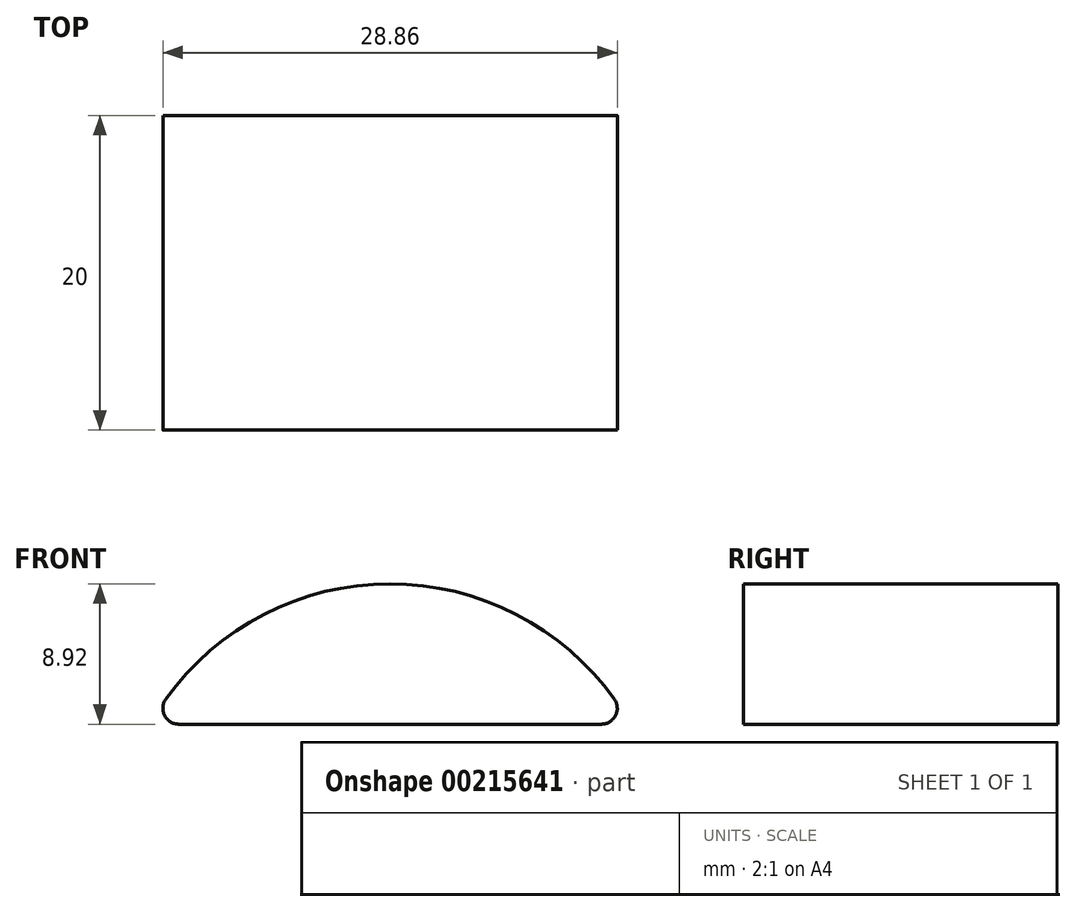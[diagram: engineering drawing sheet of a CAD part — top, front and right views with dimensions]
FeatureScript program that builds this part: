
annotation { "Feature Type Name" : "Feature", "Feature Type Description" : "" }
export const myFeature = defineFeature(function(context is Context, id is Id, definition is map)
    precondition{}
    {
        {
            var Q0;
            Q0=qCreatedBy(makeId("Front.planeOp"),FACE);
            var sketch = newSketch(context, id + "F0", { "sketchPlane" : qUnion([Q0])});
            skLineSegment(sketch, "E0", {"start": v(-13.43, 0) * mm, "end": v(13.43, 0) * mm});
            skArc(sketch, "E1", {"start": v(14.25, 1.58) * mm, "mid": v(0, 8.92) * mm, "end": v(-14.25, 1.58) * mm});
            skPoint(sketch, "E2.visualSharp", {"position": v(-15.25, 0) * mm});
            skArc(sketch, "E2.filletArc", {"start": v(-14.25, 1.58) * mm, "mid": v(-14.32, 0.54) * mm, "end": v(-13.43, 0) * mm});
            skPoint(sketch, "E3.visualSharp", {"position": v(15.25, 0) * mm});
            skArc(sketch, "E3.filletArc", {"start": v(13.43, 0) * mm, "mid": v(14.32, 0.54) * mm, "end": v(14.25, 1.58) * mm});
            skPoint(sketch, "E4", {"position": v(0, 0) * mm});
            skSolve(sketch);
        }
        {
            var Q0;
            Q0 = qSketchRegion(id + "F0", true);
            extrude(context, id + "F1", {"entities" : qUnion([Q0]), "depth" : 20 * mm});
        }
    });
